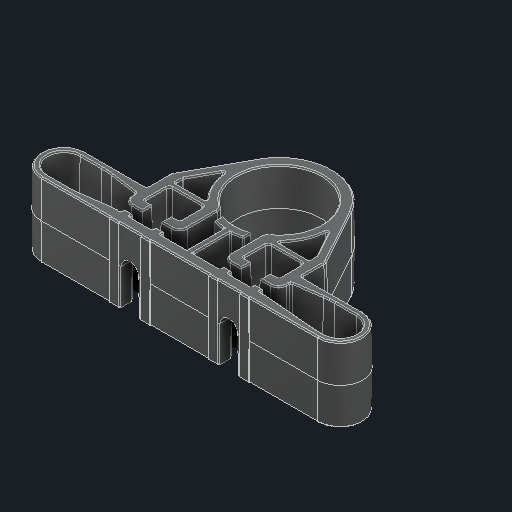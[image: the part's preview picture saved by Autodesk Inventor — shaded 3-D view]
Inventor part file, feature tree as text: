
AUTODESK INVENTOR PART (.ipt)
format: ipt  version: 2025 (Build 290162000, 162)  size: 1,221,120 bytes
history: native  units: in
note: dims shown in document units (in); Inventor stores cm internally (conversion verified against a paired STEP export)
features: fillet x1
ambient origin geometry x8: Origin, YZ Plane, XZ Plane, XY Plane, X Axis, Y Axis, Z Axis, Center Point
bodies: Solid1 (feature_tree)
feature tree (1):
  fillet  "Fillet26"  [1 undecoded]
note: 1 required parameter value undecoded (feature->parameter linkage not recoverable at this tier; creation-order binding heuristic only, values carry confidence <= 0.55)
